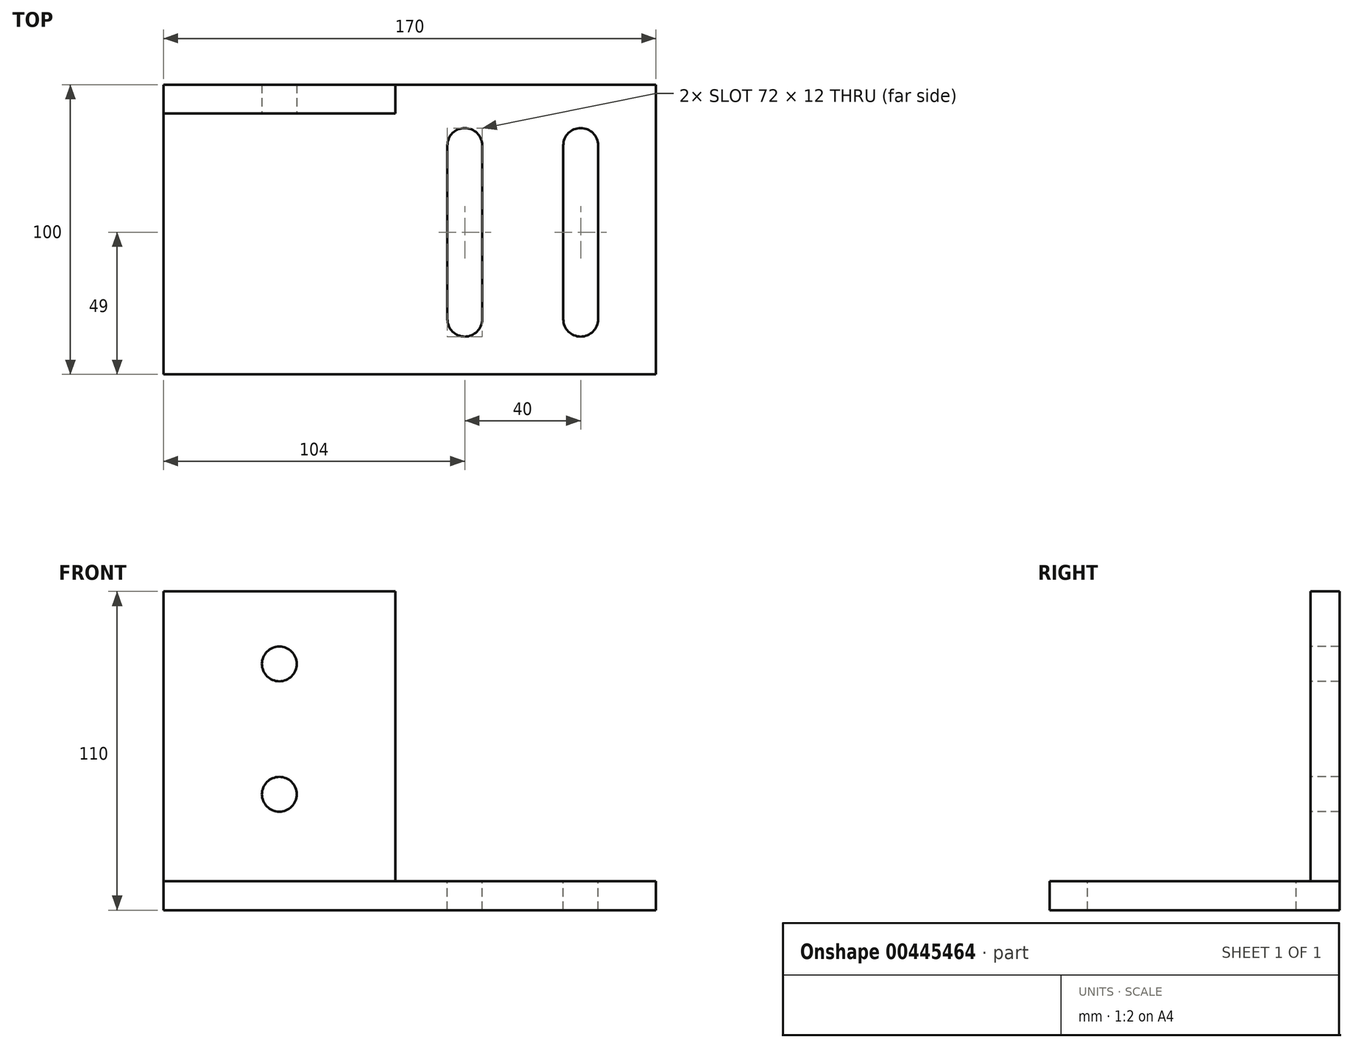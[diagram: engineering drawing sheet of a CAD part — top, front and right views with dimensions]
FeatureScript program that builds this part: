
annotation { "Feature Type Name" : "Feature", "Feature Type Description" : "" }
export const myFeature = defineFeature(function(context is Context, id is Id, definition is map)
    precondition{}
    {
        {
            var Q0;
            Q0=qCreatedBy(makeId("Front.planeOp"),FACE);
            var sketch = newSketch(context, id + "F0", { "sketchPlane" : qUnion([Q0])});
            skLineSegment(sketch, "E0.bottom", {"start": v(40, 50) * mm, "end": v(-40, 50) * mm});
            skLineSegment(sketch, "E0.top", {"start": v(40, -50) * mm, "end": v(-40, -50) * mm});
            skLineSegment(sketch, "E0.left", {"start": v(40, 50) * mm, "end": v(40, -50) * mm});
            skLineSegment(sketch, "E0.right", {"start": v(-40, 50) * mm, "end": v(-40, -50) * mm});
            skPoint(sketch, "E0.middle", {"position": v(0, 0) * mm});
            skSolve(sketch);
        }
        {
            var Q0;
            Q0 = qSketchRegion(id + "F0", true);
            extrude(context, id + "F1", {"entities" : qUnion([Q0]), "endBound" : BoundingType.SYMMETRIC, "depth" : 10 * mm, "offsetDistance" : 25 * mm});
        }
        {
            var Q0;
            Q0=makeQuery(id+"F1.opExtrude","SWEPT_FACE",FACE,{"disambiguationData":[OSD([sQuery(id+"F0.wireOp",EDGE,"E0.top")])]});
            var sketch = newSketch(context, id + "F2", { "sketchPlane" : qUnion([Q0])});
            skLineSegment(sketch, "E1.bottom", {"start": v(-40, -5) * mm, "end": v(130, -5) * mm});
            skLineSegment(sketch, "E1.top", {"start": v(-40, 95) * mm, "end": v(130, 95) * mm});
            skLineSegment(sketch, "E1.left", {"start": v(-40, -5) * mm, "end": v(-40, 95) * mm});
            skLineSegment(sketch, "E1.right", {"start": v(130, -5) * mm, "end": v(130, 95) * mm});
            skSolve(sketch);
        }
        {
            var Q0;
            Q0 = qSketchRegion(id + "F2", true);
            extrude(context, id + "F3", {"entities" : qUnion([Q0]), "operationType" : NewBodyOperationType.ADD, "depth" : 10 * mm, "offsetDistance" : 25 * mm});
        }
        {
            var Q0;
            Q0=makeQuery(id+"F1.opExtrude","CAP_FACE",FACE,{"disambiguationData":[OSD([sQuery(id+"F0.wireOp",EDGE,"E0.bottom"),sQuery(id+"F0.wireOp",EDGE,"E0.top"),sQuery(id+"F0.wireOp",EDGE,"E0.left"),sQuery(id+"F0.wireOp",EDGE,"E0.right")])],"isStart":false});
            var sketch = newSketch(context, id + "F4", { "sketchPlane" : qUnion([Q0])});
            skCircle(sketch, "E2", {"center": v(0, 25) * mm, "radius": 6 * mm});
            skCircle(sketch, "E3.0.1.0", {"center": v(0, -20) * mm, "radius": 6 * mm});
            skLineSegment(sketch, "E3.direction1", {"start": v(0, 25) * mm, "end": v(25, 25) * mm, "construction": true});
            skLineSegment(sketch, "E3.direction2", {"start": v(0, 25) * mm, "end": v(0, -20) * mm, "construction": true});
            skSolve(sketch);
        }
        {
            var Q0;
            Q0 = qSketchRegion(id + "F4", true);
            extrude(context, id + "F5", {"entities" : qUnion([Q0]), "operationType" : NewBodyOperationType.ADD, "depth" : 10 * mm, "offsetDistance" : 25 * mm});
        }
        {
            var Q0;
            Q0=makeQuery(id+"F3.opExtrude","CAP_FACE",FACE,{"disambiguationData":[OSD([sQuery(id+"F2.wireOp",EDGE,"E1.bottom"),sQuery(id+"F2.wireOp",EDGE,"E1.top"),sQuery(id+"F2.wireOp",EDGE,"E1.left"),sQuery(id+"F2.wireOp",EDGE,"E1.right")])],"isStart":true});
            var sketch = newSketch(context, id + "F6", { "sketchPlane" : qUnion([Q0])});
            skLineSegment(sketch, "E4.bottom", {"start": v(104, -10) * mm, "end": v(104, -10) * mm});
            skLineSegment(sketch, "E4.top", {"start": v(104, -82) * mm, "end": v(104, -82) * mm});
            skLineSegment(sketch, "E4.left", {"start": v(98, -16) * mm, "end": v(98, -76) * mm});
            skLineSegment(sketch, "E4.right", {"start": v(110, -16) * mm, "end": v(110, -76) * mm});
            skPoint(sketch, "E5.visualSharp", {"position": v(98, -10) * mm});
            skArc(sketch, "E5.filletArc", {"start": v(104, -10) * mm, "mid": v(99.76, -11.76) * mm, "end": v(98, -16) * mm});
            skPoint(sketch, "E6.visualSharp", {"position": v(110, -10) * mm});
            skArc(sketch, "E6.filletArc", {"start": v(110, -16) * mm, "mid": v(108.24, -11.76) * mm, "end": v(104, -10) * mm});
            skPoint(sketch, "E7.visualSharp", {"position": v(110, -82) * mm});
            skArc(sketch, "E7.filletArc", {"start": v(104, -82) * mm, "mid": v(108.24, -80.24) * mm, "end": v(110, -76) * mm});
            skPoint(sketch, "E8.visualSharp", {"position": v(98, -82) * mm});
            skArc(sketch, "E8.filletArc", {"start": v(98, -76) * mm, "mid": v(99.76, -80.24) * mm, "end": v(104, -82) * mm});
            skLineSegment(sketch, "E9.1.0.0", {"start": v(58, -16) * mm, "end": v(58, -76) * mm});
            skLineSegment(sketch, "E9.1.0.1", {"start": v(70, -16) * mm, "end": v(70, -76) * mm});
            skArc(sketch, "E9.1.0.2", {"start": v(70, -16) * mm, "mid": v(68.24, -11.76) * mm, "end": v(64, -10) * mm});
            skArc(sketch, "E9.1.0.3", {"start": v(64, -10) * mm, "mid": v(59.76, -11.76) * mm, "end": v(58, -16) * mm});
            skArc(sketch, "E9.1.0.4", {"start": v(58, -76) * mm, "mid": v(59.76, -80.24) * mm, "end": v(64, -82) * mm});
            skArc(sketch, "E9.1.0.5", {"start": v(64, -82) * mm, "mid": v(68.24, -80.24) * mm, "end": v(70, -76) * mm});
            skLineSegment(sketch, "E9.direction1", {"start": v(98, -76) * mm, "end": v(58, -76) * mm, "construction": true});
            skSolve(sketch);
        }
        {
            var Q0;
            Q0 = qSketchRegion(id + "F6", true);
            extrude(context, id + "F7", {"entities" : qUnion([Q0]), "operationType" : NewBodyOperationType.REMOVE, "oppositeDirection" : true, "depth" : 25 * mm, "offsetDistance" : 25 * mm});
        }
        {
            var Q0;
            Q0=makeQuery(id+"F5.opExtrude","CAP_FACE",FACE,{"disambiguationData":[OSD([sQuery(id+"F4.wireOp",EDGE,"E2")])],"isStart":false});
            var Q1;
            Q1=makeQuery(id+"F5.opExtrude","CAP_FACE",FACE,{"disambiguationData":[OSD([sQuery(id+"F4.wireOp",EDGE,"E3.0.1.0")])],"isStart":false});
            extrude(context, id + "F8", {"entities" : qUnion([Q0, Q1]), "operationType" : NewBodyOperationType.REMOVE, "oppositeDirection" : true, "depth" : 50 * mm, "offsetDistance" : 25 * mm});
        }
    });
